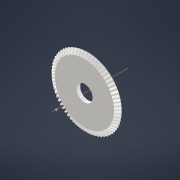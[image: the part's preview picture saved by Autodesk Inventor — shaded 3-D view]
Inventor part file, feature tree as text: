
AUTODESK INVENTOR PART (.ipt)
format: ipt  version: 2022 (Build 260153000, 153)  size: 864,256 bytes
history: native  units: mm
features: other x24, loft x2, pattern_circular x2, sketch x2, extrude x1
ambient origin geometry x6: Origin, XZ Plane, X Axis, Y Axis, Z Axis, Center Point
bodies: Solid1 (feature_tree)
feature tree (31):
  other  "Top Point"
  other  "Mesh Plane2"
  other  "Teeth Body"
  other  "Start Point"
  other  "Tooth Plane"
  other  "Start Sketch"
  other  "End Point"
  other  "3D Sketch Right"
  other  "End Plane Right"
  loft  "Loft Right"
  pattern_circular  "Circular Pattern Right"  [2 undecoded]
  other  "3D Sketch Left"
  other  "End Plane Left"
  loft  "Loft Left"
  pattern_circular  "Circular Pattern Left"  Angle=90.0deg  [1 undecoded]
  other  "Fix Body"
  extrude  "Extrusion1"  Depth=10.0mm
  other  "Mesh Plane"
  other  "Top Plane"
  other  "Teeth Body Sketch"
  other  "End Plane"
  other  "End Sketch"
  other  "Helical Curve Left"
  other  "End Sketch Left"
  other  "Body Sketch"
  sketch  "Sketch6"  dims[d0=128.0mm d1=124.807579mm]
  other  "Srf1"
  other  "Helical Curve Right"
  other  "End Sketch Right"
  sketch  "Sketch8"  dims[d2=130.660351mm d3=10.0mm d4=55.50647mm d5=90.0deg d7=33.607126mm d8=33.101065mm d9=84.536747mm d11=10.22mm d12=29.599507mm d15=29.153794mm d16=74.455818mm d17=0.0mm d18=90.0deg d19=0.0mm d20=90.0deg d21=640.0mm d22=360.0deg d26=670.288624mm d27=6.797197mm d28=128.0mm d29=-8.43185mm d30=29.599507mm d31=29.153794mm d32=74.455818mm d35=0.0mm d37=0.0mm d39=0.0mm d40=90.0deg d41=640.0mm d42=360.0deg d46=90.0deg d47=90.0deg d48=0.0mm d49=0.0mm d50=90.0deg d51=0.490874mm d52=0.0mm d53=0.0mm d54=0.0mm d56=38.380865mm d57=99.547902mm d58=93.299902mm d59=87.676908mm d60=82.173976mm d61=87.676908mm d62=82.173976mm d65=670.288624mm d66=31.5mm d67=128.0mm d68=-8.43185mm d69=6.797197mm d70=29.153794mm d71=74.455818mm d72=29.599507mm d73=82.173976mm d74=87.676908mm d75=0.0mm d77=0.0mm d79=0.0mm d80=90.0deg d81=640.0mm d82=360.0deg d84=10.0mm d85=20.0mm d86=20.0mm d87=10.0mm d88=0.0mm d89=0.0mm d90=90.0deg d91=90.0deg d92=90.0deg d93=90.0deg d94=30.0mm d95=0.0mm d96=0.0mm]
  other  "Pitch Diameter"
note: 3 required parameter values undecoded (feature->parameter linkage not recoverable at this tier; creation-order binding heuristic only, values carry confidence <= 0.55)
